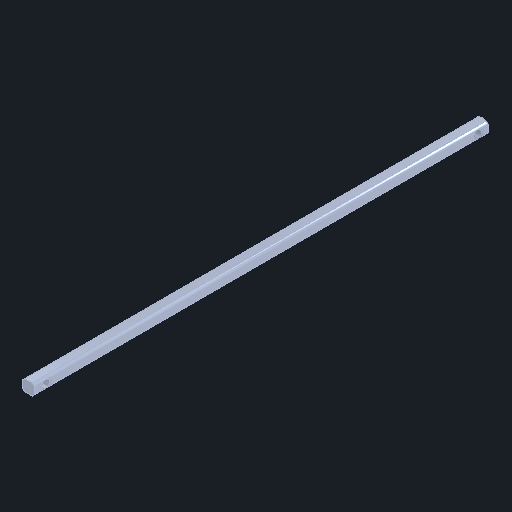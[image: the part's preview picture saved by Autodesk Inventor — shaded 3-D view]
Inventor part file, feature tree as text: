
AUTODESK INVENTOR PART (.ipt)
format: ipt  version: 2025 (Build 290162000, 162)  size: 166,912 bytes
history: native  units: in
note: dims shown in document units (in); Inventor stores cm internally (conversion verified against a paired STEP export)
features: extrude x3, sketch x3, thicken_offset x1, other x1
ambient origin geometry x8: Origin, YZ Plane, XZ Plane, XY Plane, X Axis, Y Axis, Z Axis, Center Point
bodies: Solid1 (feature_tree)
feature tree (8):
  extrude  "Extrusion1"  Depth=12.1875in
  thicken_offset  "Thicken1"
  extrude  "Extrusion2"  Depth=14.125in
  extrude  "Extrusion3"  Depth=0.165in
  sketch  "Sketch2"  dims[d0=0.0625in d1=0.0in d2=12.1875in]
  sketch  "Sketch3"  dims[d3=12.125in d4=14.125in]
  sketch  "Sketch4"  dims[d5=0.0in d6=0.165in d7=0.165in d8=1.0in d9=0.0in]
  other  "Cut-Revolve3"
